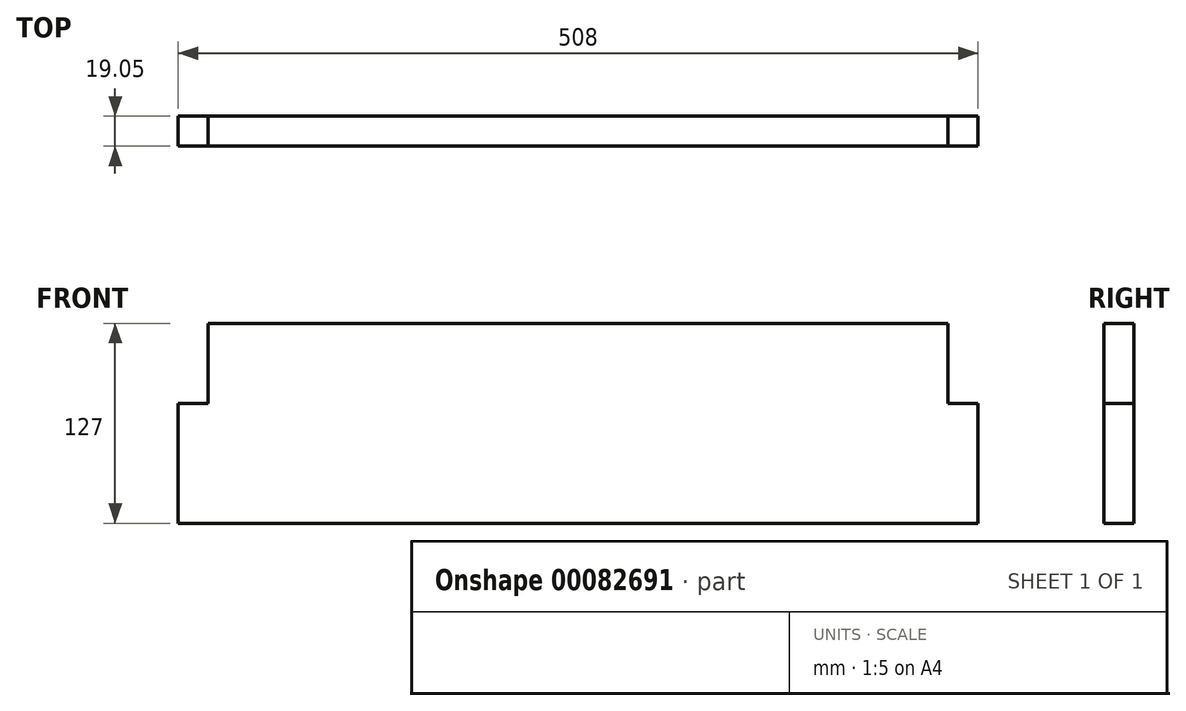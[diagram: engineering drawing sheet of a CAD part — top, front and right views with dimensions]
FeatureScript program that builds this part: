
annotation { "Feature Type Name" : "Feature", "Feature Type Description" : "" }
export const myFeature = defineFeature(function(context is Context, id is Id, definition is map)
    precondition{}
    {
        {
            var Q0;
            Q0=qCreatedBy(makeId("Front.planeOp"),FACE);
            var sketch = newSketch(context, id + "F0", { "sketchPlane" : qUnion([Q0])});
            skLineSegment(sketch, "E0.top", {"start": v(-393.5, -146.23) * mm, "end": v(114.5, -146.23) * mm});
            skLineSegment(sketch, "E0.left", {"start": v(-393.5, -70.03) * mm, "end": v(-393.5, -146.23) * mm});
            skLineSegment(sketch, "E0.right", {"start": v(114.5, -70.03) * mm, "end": v(114.5, -146.23) * mm});
            skLineSegment(sketch, "E1.0", {"start": v(-393.5, -70.03) * mm, "end": v(-374.45, -70.03) * mm});
            skLineSegment(sketch, "E2.0", {"start": v(-374.45, -19.23) * mm, "end": v(-374.45, -70.03) * mm});
            skLineSegment(sketch, "E3.0", {"start": v(95.45, -19.23) * mm, "end": v(95.45, -70.03) * mm});
            skLineSegment(sketch, "E4.trimOffspring", {"start": v(95.45, -70.03) * mm, "end": v(114.5, -70.03) * mm});
            skLineSegment(sketch, "E5.0", {"start": v(-374.45, -19.23) * mm, "end": v(95.45, -19.23) * mm});
            skSolve(sketch);
        }
        {
            var Q0;
            Q0=qSketchRegion(id+"F0",true);
            extrude(context, id + "F1", {"entities" : qUnion([Q0]), "depth" : 19.05 * mm});
        }
    });
